# Revit family: Overhead-Sect_HAAS_Res_Alum_5000
name_source: partatom
category: Doors
units: mm (PartAtom-declared; Revit-internal decimal feet)

## family parameters
Always vertical = Yes
Cut with Voids When Loaded = No
Host = Wall
OmniClass Number = 23.30.10.17.37.14
OmniClass Title = Sectional Overhead Doors
Room Calculation Point = No
Shared = No

## types (8) — shared parameters
AAMA Designation = as Specified
Assembly Code = B2030410
End Stile Type = Extruded End Cap
Function = Exterior
Height = 0' - 0"
Interior Skin = Aluminum Woodgrain
Keynote = 08360
Manufacturer = Haas Door Co.
Manufacturer Fax = 800-874-4227
Manufacturer Website = http://www.haasdoor.com
Max Height = 12' - 0"
Max Width = 16' - 0"
Operation = Overhead Sectional
Product Data = http://www.arcat.com
Revision = R1_2015-11
Roof Incline Default = 0.00°
Rough Height = 0' - 0"
Rough Width = 0' - 0"
Sales Information = http://www.haasdoor.com
Standards Conformance = as Specified
Thickness = 0' - 0"
URL = http://www.haasdoor.com
Wall Closure = By host
Width = 0' - 0"
rearspring = No
zero-valued in all types: Cost, Expected Lifespan (Years), Maintenance Schedule (Months), U Value, Warranty Duration (Years)

## per-type parameters (varying)
| type | Description | Exterior Skin | Model | Panel Thickness | R-Value |
| Model 5780 Raised 1.75in | Haas 5700 Series Residential Insulated Overhead Sectional Door - 5780 as Specified | Raised Panel Woodgrain Aluminum | 5780 | 0' - 1 3/4" | 16.18 |
| Model 5770 Raised Ranch 1.75in | Haas 5700 Series Residential Insulated Overhead Sectional Door - 5770 as Specified | Raised Ranch Panel Woodgrain Aluminum | 5770 | 0' - 1 3/4" | 16.18 |
| Model 5712 V Groove 1.75in | Haas 5700 Series Residential Insulated Overhead Sectional Door - 5712 as Specified | V Groove Woodgrain Aluminum | 5712 | 0' - 1 3/4" | 16.18 |
| Model 5710 Flush 1.75in | Haas 5700 Series Residential Insulated Overhead Sectional Door - 5710 as Specified | Flush Woodgrain Aluminum | 5710 | 0' - 1 3/4" | 16.18 |
| Model 5280 Raised 2in | Haas 5200 Series Residential Insulated Overhead Sectional Door - 5280 as Specified | Raised Panel Woodgrain Aluminum | 5280 | 0' - 2" | 17.66 |
| Model 5270 Raised Ranch 2in | Haas 5200 Series Residential Insulated Overhead Sectional Door - 5270 as Specified | Raised Ranch Panel Woodgrain Aluminum | 5270 | 0' - 2" | 17.66 |
| Model 5212 V Groove 2in | Haas 5200 Series Residential Insulated Overhead Sectional Door - 5212 as Specified | V Groove Woodgrain Aluminum | 5212 | 0' - 2" | 17.66 |
| Model 5210 Flush 2in | Haas 5200 Series Residential Insulated Overhead Sectional Door - 5210 as Specified | Flush Woodgrain Aluminum | 5210 | 0' - 2" | 17.66 |

## geometry (parser evidence)
native form markers: Sweep x20
no freeform markers — native parametric forms only
